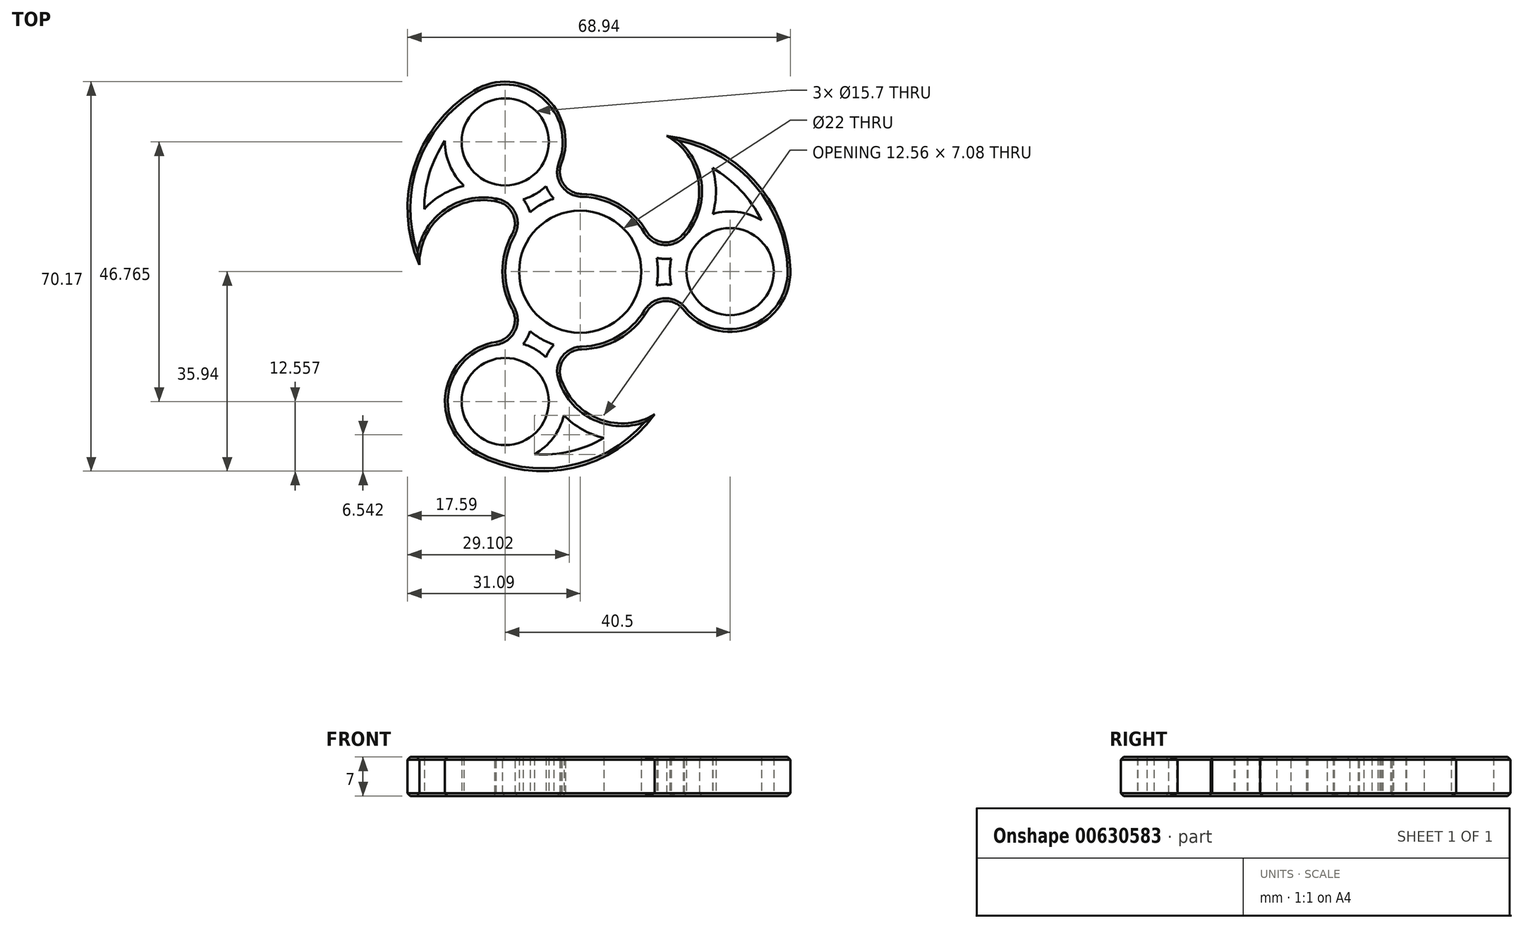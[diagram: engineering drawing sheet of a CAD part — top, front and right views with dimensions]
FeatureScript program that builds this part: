
annotation { "Feature Type Name" : "Feature", "Feature Type Description" : "" }
export const myFeature = defineFeature(function(context is Context, id is Id, definition is map)
    precondition{}
    {
        {
            var Q0;
            Q0=qCreatedBy(makeId("Top.planeOp"),FACE);
            var sketch = newSketch(context, id + "F0", { "sketchPlane" : qUnion([Q0])});
            skCircle(sketch, "E0", {"center": v(0, 0) * mm, "radius": 11 * mm});
            skCircle(sketch, "E1", {"center": v(0, 0) * mm, "radius": 27 * mm, "construction": true});
            skCircle(sketch, "E2", {"center": v(27, 0) * mm, "radius": 7.85 * mm});
            skArc(sketch, "E3.0", {"start": v(18.54, -6.79) * mm, "mid": v(30.74, -10.19) * mm, "end": v(37.85, 0.3) * mm});
            skCircle(sketch, "E4", {"center": v(0, 0) * mm, "radius": 29 * mm, "construction": true});
            skLineSegment(sketch, "E5", {"start": v(27, 0) * mm, "end": v(15.57, 24.46) * mm, "construction": true});
            skArc(sketch, "E6", {"start": v(37.85, 0.3) * mm, "mid": v(31.24, 16.55) * mm, "end": v(15.57, 24.46) * mm});
            skArc(sketch, "E7", {"start": v(18.72, 7) * mm, "mid": v(21.26, 16.48) * mm, "end": v(15.57, 24.46) * mm});
            skArc(sketch, "E8.0", {"start": v(13.78, -2.49) * mm, "mid": v(14, 0) * mm, "end": v(13.78, 2.49) * mm});
            skArc(sketch, "E9", {"start": v(12, 7.23) * mm, "mid": v(15.15, 5.3) * mm, "end": v(18.54, 6.79) * mm});
            skArc(sketch, "E10.0", {"start": v(13.78, 2.49) * mm, "mid": v(15.09, 2.3) * mm, "end": v(16.41, 2.36) * mm});
            skArc(sketch, "E11.MirrorCS", {"start": v(13.78, -2.49) * mm, "mid": v(15.09, -2.3) * mm, "end": v(16.41, -2.36) * mm});
            skArc(sketch, "E12.MirrorCS", {"start": v(12, -7.23) * mm, "mid": v(15.15, -5.3) * mm, "end": v(18.54, -6.79) * mm});
            skArc(sketch, "E13.trimOffspring", {"start": v(16.41, 2.36) * mm, "mid": v(16.15, 0) * mm, "end": v(16.41, -2.36) * mm});
            skArc(sketch, "E14.trimOffspring", {"start": v(12, 7.23) * mm, "mid": v(7, 12.12) * mm, "end": v(0.26, 14) * mm});
            skArc(sketch, "E15.0", {"start": v(32.61, 9.28) * mm, "mid": v(28.91, 14.65) * mm, "end": v(23.8, 18.7) * mm});
            skArc(sketch, "E16.0", {"start": v(23.86, 10.39) * mm, "mid": v(24.44, 14.55) * mm, "end": v(23.8, 18.7) * mm});
            skArc(sketch, "E17.trimOffspring", {"start": v(32.61, 9.28) * mm, "mid": v(28.36, 10.77) * mm, "end": v(23.86, 10.39) * mm});
            skArc(sketch, "E18.1.0", {"start": v(-24.35, 23.6) * mm, "mid": v(-23.5, 19.17) * mm, "end": v(-20.93, 15.47) * mm});
            skArc(sketch, "E18.1.1", {"start": v(-20.93, 15.47) * mm, "mid": v(-24.82, 13.9) * mm, "end": v(-28.1, 11.26) * mm});
            skArc(sketch, "E18.1.2", {"start": v(0.26, 14) * mm, "mid": v(-2.98, 15.77) * mm, "end": v(-3.39, 19.45) * mm});
            skArc(sketch, "E18.1.3", {"start": v(-4.74, 13.17) * mm, "mid": v(-5.55, 14.22) * mm, "end": v(-6.16, 15.4) * mm});
            skArc(sketch, "E18.1.4", {"start": v(-9.04, 10.69) * mm, "mid": v(-9.54, 11.92) * mm, "end": v(-10.25, 13.03) * mm});
            skArc(sketch, "E18.1.5", {"start": v(-12.25, 6.77) * mm, "mid": v(-12.17, 10.47) * mm, "end": v(-15.15, 12.66) * mm});
            skArc(sketch, "E18.1.6", {"start": v(-4.74, 13.17) * mm, "mid": v(-7, 12.12) * mm, "end": v(-9.04, 10.69) * mm});
            skArc(sketch, "E18.1.7", {"start": v(-15.43, 12.7) * mm, "mid": v(-24.9, 10.17) * mm, "end": v(-28.97, 1.26) * mm});
            skArc(sketch, "E18.1.8", {"start": v(-19.18, 32.63) * mm, "mid": v(-29.96, 18.78) * mm, "end": v(-28.97, 1.26) * mm});
            skArc(sketch, "E18.1.9", {"start": v(-3.39, 19.45) * mm, "mid": v(-6.55, 31.71) * mm, "end": v(-19.18, 32.63) * mm});
            skCircle(sketch, "E18.1.10", {"center": v(-13.5, 23.38) * mm, "radius": 7.85 * mm});
            skArc(sketch, "E18.1.11", {"start": v(-24.35, 23.6) * mm, "mid": v(-27.14, 17.71) * mm, "end": v(-28.1, 11.26) * mm});
            skArc(sketch, "E18.1.12", {"start": v(-10.25, 13.03) * mm, "mid": v(-8.07, 13.99) * mm, "end": v(-6.16, 15.4) * mm});
            skArc(sketch, "E18.2.0", {"start": v(-8.27, -32.89) * mm, "mid": v(-4.85, -29.94) * mm, "end": v(-2.94, -25.86) * mm});
            skArc(sketch, "E18.2.1", {"start": v(-2.94, -25.86) * mm, "mid": v(0.38, -28.44) * mm, "end": v(4.3, -29.96) * mm});
            skArc(sketch, "E18.2.2", {"start": v(-12.25, -6.77) * mm, "mid": v(-12.17, -10.47) * mm, "end": v(-15.15, -12.66) * mm});
            skArc(sketch, "E18.2.3", {"start": v(-9.04, -10.69) * mm, "mid": v(-9.54, -11.92) * mm, "end": v(-10.25, -13.03) * mm});
            skArc(sketch, "E18.2.4", {"start": v(-4.74, -13.17) * mm, "mid": v(-5.55, -14.22) * mm, "end": v(-6.16, -15.4) * mm});
            skArc(sketch, "E18.2.5", {"start": v(0.26, -14) * mm, "mid": v(-2.98, -15.77) * mm, "end": v(-3.39, -19.45) * mm});
            skArc(sketch, "E18.2.6", {"start": v(-9.04, -10.69) * mm, "mid": v(-7, -12.12) * mm, "end": v(-4.74, -13.17) * mm});
            skArc(sketch, "E18.2.7", {"start": v(-3.29, -19.71) * mm, "mid": v(3.64, -26.65) * mm, "end": v(13.4, -25.72) * mm});
            skArc(sketch, "E18.2.8", {"start": v(-18.66, -32.92) * mm, "mid": v(-1.28, -35.33) * mm, "end": v(13.4, -25.72) * mm});
            skArc(sketch, "E18.2.9", {"start": v(-15.15, -12.66) * mm, "mid": v(-24.2, -21.53) * mm, "end": v(-18.66, -32.92) * mm});
            skCircle(sketch, "E18.2.10", {"center": v(-13.5, -23.38) * mm, "radius": 7.85 * mm});
            skArc(sketch, "E18.2.11", {"start": v(-8.27, -32.89) * mm, "mid": v(-1.77, -32.36) * mm, "end": v(4.3, -29.96) * mm});
            skArc(sketch, "E18.2.12", {"start": v(-6.16, -15.4) * mm, "mid": v(-8.08, -13.99) * mm, "end": v(-10.25, -13.03) * mm});
            skArc(sketch, "E19.trimOffspring", {"start": v(-12.25, 6.77) * mm, "mid": v(-14, 0) * mm, "end": v(-12.25, -6.77) * mm});
            skArc(sketch, "E20.trimOffspring", {"start": v(0.26, -14) * mm, "mid": v(7, -12.12) * mm, "end": v(12, -7.23) * mm});
            skLineSegment(sketch, "E21", {"start": v(18.54, 6.79) * mm, "end": v(18.72, 7) * mm});
            skLineSegment(sketch, "E22", {"start": v(-15.15, 12.66) * mm, "end": v(-15.43, 12.7) * mm});
            skLineSegment(sketch, "E23", {"start": v(-3.29, -19.71) * mm, "end": v(-3.39, -19.45) * mm});
            skSolve(sketch);
        }
        {
            var Q0;
            Q0=makeQuery(id+"F0.imprint","IMPRINT",FACE,{"disambiguationData":[TD([[makeQuery(id+"F0.imprint","IMPRINT",EDGE,{"derivedFrom":sQuery(id+"F0.wireOp",EDGE,"E0")}),-1.0]])]});
            extrude(context, id + "F1", {"entities" : qUnion([Q0]), "endBound" : BoundingType.SYMMETRIC, "depth" : 7 * mm, "offsetDistance" : 25 * mm});
        }
        {
            var Q0;
            Q0=makeQuery(id+"F1.opExtrude","CAP_EDGE",EDGE,{"disambiguationData":[OSD([sQuery(id+"F0.wireOp",EDGE,"E20.trimOffspring")])],"isStart":true});
            var Q1;
            Q1=makeQuery(id+"F1.opExtrude","CAP_EDGE",EDGE,{"disambiguationData":[OSD([sQuery(id+"F0.wireOp",EDGE,"E18.2.9")])],"isStart":true});
            var Q2;
            Q2=makeQuery(id+"F1.opExtrude","CAP_EDGE",EDGE,{"disambiguationData":[OSD([sQuery(id+"F0.wireOp",EDGE,"E18.2.7")])],"isStart":true});
            var Q3;
            Q3=makeQuery(id+"F1.opExtrude","CAP_EDGE",EDGE,{"disambiguationData":[OSD([sQuery(id+"F0.wireOp",EDGE,"E18.1.7")])],"isStart":true});
            var Q4;
            Q4=makeQuery(id+"F1.opExtrude","CAP_EDGE",EDGE,{"disambiguationData":[OSD([sQuery(id+"F0.wireOp",EDGE,"E18.1.8")])],"isStart":true});
            var Q5;
            Q5=makeQuery(id+"F1.opExtrude","CAP_EDGE",EDGE,{"disambiguationData":[OSD([sQuery(id+"F0.wireOp",EDGE,"E7")])],"isStart":true});
            var Q6;
            Q6=makeQuery(id+"F1.opExtrude","CAP_EDGE",EDGE,{"disambiguationData":[OSD([sQuery(id+"F0.wireOp",EDGE,"E7")])],"isStart":false});
            var Q7;
            Q7=makeQuery(id+"F1.opExtrude","CAP_EDGE",EDGE,{"disambiguationData":[OSD([sQuery(id+"F0.wireOp",EDGE,"E14.trimOffspring")])],"isStart":false});
            var Q8;
            Q8=makeQuery(id+"F1.opExtrude","CAP_EDGE",EDGE,{"disambiguationData":[OSD([sQuery(id+"F0.wireOp",EDGE,"E6")])],"isStart":false});
            var Q9;
            Q9=makeQuery(id+"F1.opExtrude","CAP_EDGE",EDGE,{"disambiguationData":[OSD([sQuery(id+"F0.wireOp",EDGE,"E18.2.7")])],"isStart":false});
            var Q10;
            Q10=makeQuery(id+"F1.opExtrude","CAP_EDGE",EDGE,{"disambiguationData":[OSD([sQuery(id+"F0.wireOp",EDGE,"E18.2.8")])],"isStart":false});
            var Q11;
            Q11=makeQuery(id+"F1.opExtrude","CAP_EDGE",EDGE,{"disambiguationData":[OSD([sQuery(id+"F0.wireOp",EDGE,"E18.1.7")])],"isStart":false});
            chamfer(context, id + "F2", {"entities" : qUnion([Q0, Q1, Q2, Q3, Q4, Q5, Q6, Q7, Q8, Q9, Q10, Q11]), "width" : 0.5 * mm, "tangentPropagation" : true});
        }
    });
